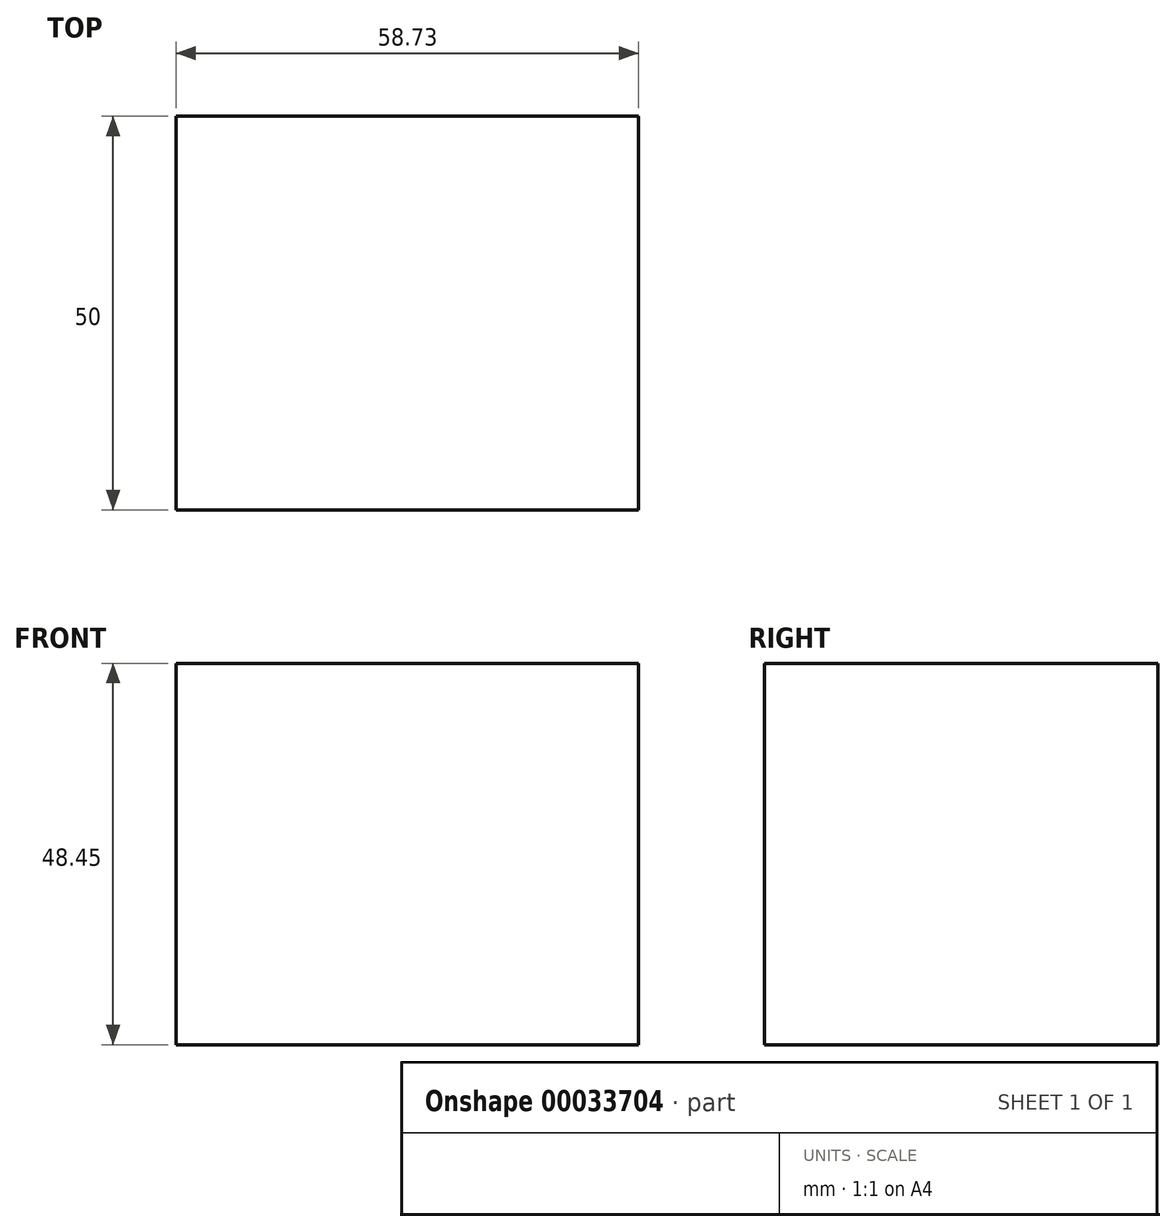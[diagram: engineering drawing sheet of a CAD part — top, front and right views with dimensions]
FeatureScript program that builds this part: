
annotation { "Feature Type Name" : "Feature", "Feature Type Description" : "" }
export const myFeature = defineFeature(function(context is Context, id is Id, definition is map)
    precondition{}
    {
        {
            var Q0;
            Q0=qCreatedBy(makeId("Front.planeOp"),FACE);
            var sketch = newSketch(context, id + "F0", { "sketchPlane" : qUnion([Q0])});
            skLineSegment(sketch, "E0.bottom", {"start": v(-32, 26) * mm, "end": v(26.74, 26) * mm});
            skLineSegment(sketch, "E0.top", {"start": v(-32, -22.45) * mm, "end": v(26.74, -22.45) * mm});
            skLineSegment(sketch, "E0.left", {"start": v(-32, 26) * mm, "end": v(-32, -22.45) * mm});
            skLineSegment(sketch, "E0.right", {"start": v(26.74, 26) * mm, "end": v(26.74, -22.45) * mm});
            skSolve(sketch);
        }
        {
            var Q0;
            Q0=makeQuery(id+"F0.imprint","IMPRINT",FACE,{"disambiguationData":[TD([[makeQuery(id+"F0.imprint","IMPRINT",EDGE,{"derivedFrom":sQuery(id+"F0.wireOp",EDGE,"E0.bottom")}),-1.0]])]});
            extrude(context, id + "F1", {"entities" : qUnion([Q0]), "endBound" : BoundingType.SYMMETRIC, "depth" : 50 * mm});
        }
        {
            var Q0;
            Q0=makeQuery(id+"F1.opExtrude","CAP_FACE",FACE,{"disambiguationData":[OSD([sQuery(id+"F0.wireOp",EDGE,"E0.bottom"),sQuery(id+"F0.wireOp",EDGE,"E0.top"),sQuery(id+"F0.wireOp",EDGE,"E0.left"),sQuery(id+"F0.wireOp",EDGE,"E0.right")])],"isStart":false});
            var sketch = newSketch(context, id + "F2", { "sketchPlane" : qUnion([Q0])});
            skCircle(sketch, "E1", {"center": v(14.8, 0) * mm, "radius": 12.84 * mm});
            skSolve(sketch);
        }
        {
            var Q0;
            {var subQ0=makeQuery(id+"F1.opExtrude","CAP_EDGE",EDGE,{"disambiguationData":[OSD([sQuery(id+"F0.wireOp",EDGE,"E0.right")])],"isStart":false});var subQ1=sQuery(id+"F2.wireOp",EDGE,"E1");var subQ3=makeQuery(id+"F2.imprint","INTERSECT",VERTEX,{"disambiguationData":[OD(0.0)],"derivedFrom":[subQ0,subQ1]});Q0=makeQuery(id+"F2.imprint","IMPRINT",FACE,{"disambiguationData":[TD([[makeQuery(id+"F2.imprint","IMPRINT",EDGE,{"disambiguationData":[TD([[subQ3,-1.0]])],"derivedFrom":subQ1}),1.0]])]});}
            extrude(context, id + "F3", {"entities" : qUnion([Q0]), "operationType" : NewBodyOperationType.ADD, "oppositeDirection" : true, "depth" : 50 * mm});
        }
    });
